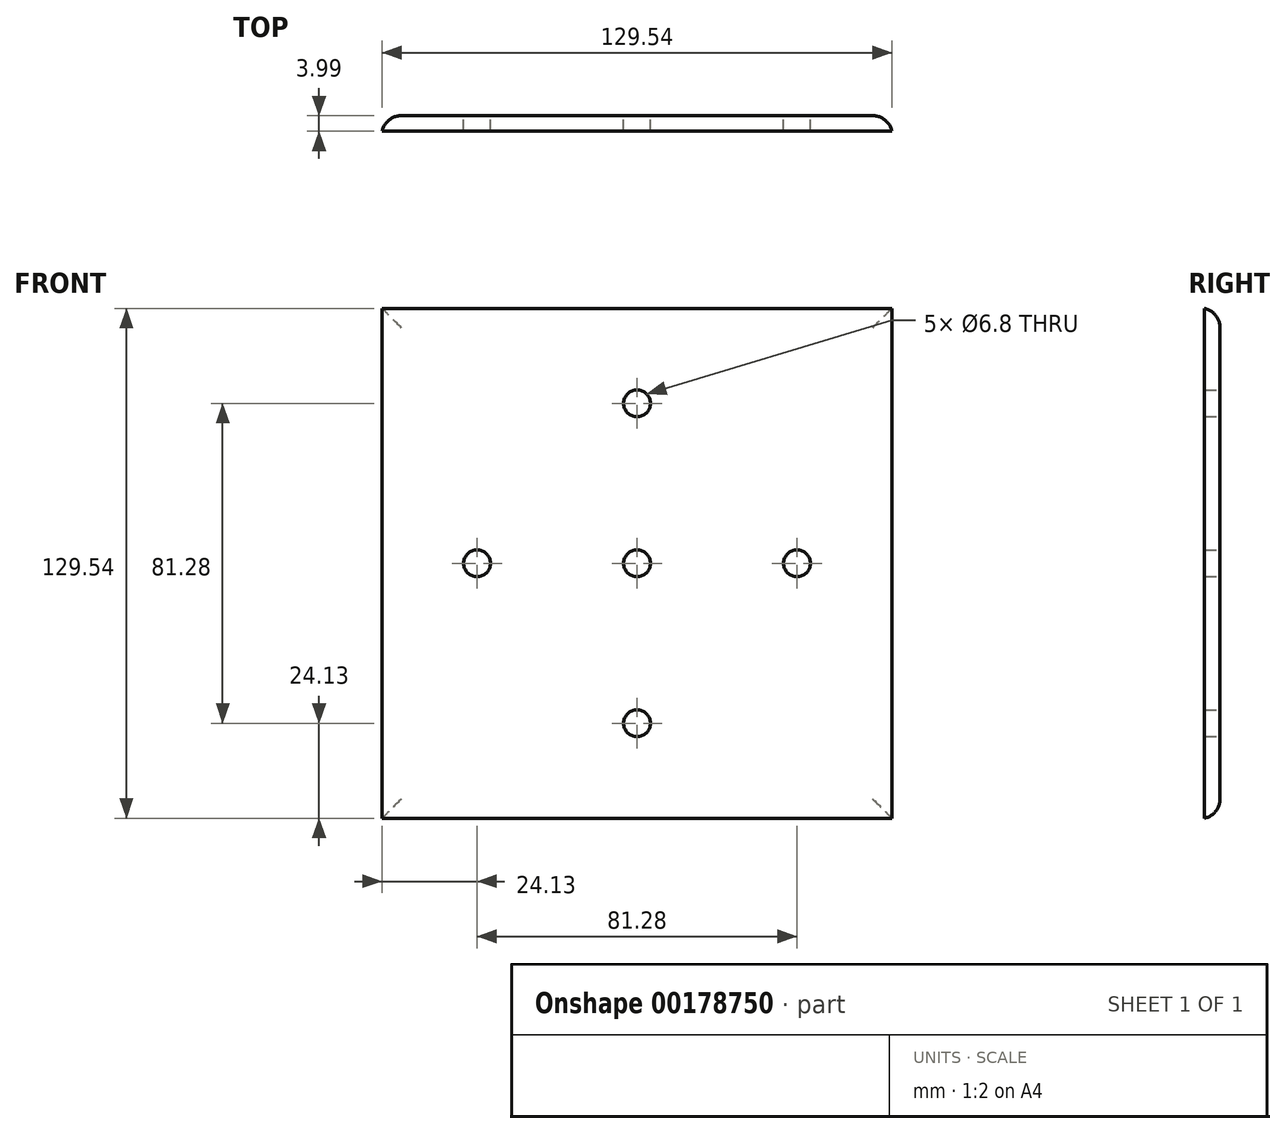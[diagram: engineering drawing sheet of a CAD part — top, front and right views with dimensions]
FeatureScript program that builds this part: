
annotation { "Feature Type Name" : "Feature", "Feature Type Description" : "" }
export const myFeature = defineFeature(function(context is Context, id is Id, definition is map)
    precondition{}
    {
        {
            var Q0;
            Q0=qCreatedBy(makeId("Front.planeOp"),FACE);
            var sketch = newSketch(context, id + "F0", { "sketchPlane" : qUnion([Q0])});
            skLineSegment(sketch, "E0.bottom", {"start": v(64.77, -64.77) * mm, "end": v(-64.77, -64.77) * mm});
            skLineSegment(sketch, "E0.top", {"start": v(64.77, 64.77) * mm, "end": v(-64.77, 64.77) * mm});
            skLineSegment(sketch, "E0.left", {"start": v(64.77, -64.77) * mm, "end": v(64.77, 64.77) * mm});
            skLineSegment(sketch, "E0.right", {"start": v(-64.77, -64.77) * mm, "end": v(-64.77, 64.77) * mm});
            skPoint(sketch, "E0.middle", {"position": v(0, 0) * mm});
            skCircle(sketch, "E1", {"center": v(0, 0) * mm, "radius": 3.4 * mm});
            skCircle(sketch, "E2", {"center": v(40.64, 0) * mm, "radius": 3.4 * mm});
            skCircle(sketch, "E3", {"center": v(0, 40.64) * mm, "radius": 3.4 * mm});
            skCircle(sketch, "E4", {"center": v(-40.64, 0) * mm, "radius": 3.4 * mm});
            skCircle(sketch, "E5.MirrorC", {"center": v(0, -40.64) * mm, "radius": 3.4 * mm});
            skSolve(sketch);
        }
        {
            var Q0;
            Q0 = qSketchRegion(id + "F0", true);
            extrude(context, id + "F1", {"entities" : qUnion([Q0]), "depth" : 4 * mm});
        }
        {
            var Q0;
            Q0=makeQuery(id+"F1.opExtrude","CAP_EDGE",EDGE,{"disambiguationData":[OSD([sQuery(id+"F0.wireOp",EDGE,"E0.right")])],"isStart":true});
            var Q1;
            Q1=makeQuery(id+"F1.opExtrude","CAP_EDGE",EDGE,{"disambiguationData":[OSD([sQuery(id+"F0.wireOp",EDGE,"E0.bottom")])],"isStart":true});
            var Q2;
            Q2=makeQuery(id+"F1.opExtrude","CAP_EDGE",EDGE,{"disambiguationData":[OSD([sQuery(id+"F0.wireOp",EDGE,"E0.left")])],"isStart":true});
            var Q3;
            Q3=makeQuery(id+"F1.opExtrude","CAP_EDGE",EDGE,{"disambiguationData":[OSD([sQuery(id+"F0.wireOp",EDGE,"E0.top")])],"isStart":true});
            fillet(context, id + "F2", {"entities" : qUnion([Q0, Q1, Q2, Q3]), "radius" : 5.08 * mm, "tangentPropagation" : true, "allowEdgeOverflow" : false});
        }
    });
